# Revit family: Pump_Commercial-Sewage_Dewatering-Zoeller-X64HD_Single_Seal_4-HH-25-40BHP_Series
name_source: partatom
category: Mechanical Equipment
revit_build: Autodesk Revit 2014 (Build: 20130308_1515(x64)
units: mm (PartAtom-declared; Revit-internal decimal feet)

## types (9) — shared parameters
Assembly Code = D2090
Connection Description = 4" Horizontal Discharge
Default Elevation = 0"
Description = Heavy Duty Solids-Handling Pumps
Discharge Diameter = 4"
Discharge Radius = 2"
Flange = ANSI B16.1 CLASS 125
Height = 48 11/32"
Hertz = 60
High Temperature (5-10 BHP) = No
Impeller Type = 2 Vane Enclosed
Installation Type = Floor Mounted
Insulation = Class F
Inverted Duty = No
Inverted Duty Submersible = No
Length = 25 5/8"
Manufacturer = Zoeller
Material = Cast Iron-Zoeller-Powder Coated Epoxy
Max. Flow @ 117' = 0 GPM
Max. Flow @ 135' = 0 GPM
Max. Stator Temp. = 311 °F
Max. Water Temp. = 104 °F
Min. Recommended Fluid Level = 36"
Moisture Detection = Moisture Sensing Probes
Motor Design Letter = NEMA B
Motor Shaft = 416 SS
Motor Thermal Shutoff = Thermal Sensors With Automatic Reset
Motor Type = Standard Submersible
NEC Locked Rotor Code = F
O-Rings (Optional) Viton = No
O-Rings and Cover Gasket = Buna-N
Operation = Non-Automatic
Phase = 3
Power Cord = 25' (7.6 m) #2-4 SO
Price = Prices may vary. Please consult Manufacturer Representative for most up-to-date price list.
Product Documentation Link = https://www.zoellerengprod.com
Product Page URL = https://www.zoellerengprod.com
RPM = 1725
Sensor Cord Size = #16-5 SO
Service Factor = 1.15
Shaft Seal (Standard) = Carbon/Ceramic
Shaft Seal Lower (Options) = Silicon Carbide
Shaft Seal Upper (Options) = Silicon Carbide
Solid Size = 4"- 3-1/8"
Tandem Seals = Standard
Trimmed Impeller = No
URL = http://www.zoellerpumps.com
Warranty Information = 36 Months (Limited)
Waste Connection = Yes
Width = 22 1/2"

## per-type parameters (varying)
| type | Amps | Apparent Load | Flow Rate | Impeller Diameter | Locked Rotor Amps (Voltage Dependant) | Max. Flow @ 45' | Max. Flow @ 60' | Max. Flow @ 85' | Max. Head | Maximum KW Input | Model | Motor | Pump Net Weight: lbs. (kg) | Voltage |
| X6424 - 230V/3Ph/64.2A/25BHP | 64 A | 14766 VA | 1130 GPM | 9 7/8" | 349 | 1130 GPM | 0 GPM | 0 GPM | 110' | 21.1 | X6424 | 25 BHP | 705 lbs. (319 kg) | 230 V |
| X6425 - 230V/3Ph/79.8A/30BHP | 80 A | 18354 VA | 1100 GPM | 10 3/8" | 416 | 0 GPM | 1100 GPM | 0 GPM | 123' | 25.2 | X6425 | 30 BHP | 730 lbs. (331 kg) | 230 V |
| X6426 - 460V/3Ph/51.7A/40BHP | 52 A | 23782 VA | 1070 GPM | 11 3/8" | 257 | 0 GPM | 0 GPM | 1070 GPM | 142' | 33.5 | X6426 | 40 BHP | 780 lbs. (354 kg) | 460 V |
| X6424 - 460V/3Ph/32.1A/25BHP | 32 A | 14766 VA | 1130 GPM | 9 7/8" | 175 | 1130 GPM | 0 GPM | 0 GPM | 110' | 21.1 | X6424 | 25 BHP | 705 lbs. (319 kg) | 460 V |
| X6424 - 575V/3Ph/25.6A/25BHP | 26 A | 14720 VA | 1130 GPM | 9 7/8" | 140 | 1130 GPM | 0 GPM | 0 GPM | 110' | 21.1 | X6424 | 25 BHP | 705 lbs. (319 kg) | 575 V |
| X6425 - 460V/3Ph/39.9A/30BHP | 40 A | 18354 VA | 1100 GPM | 10 3/8" | 208 | 0 GPM | 1100 GPM | 0 GPM | 123' | 25.2 | X6425 | 30 BHP | 730 lbs. (331 kg) | 460 V |
| X6425 - 575V/3Ph/31.9A/30BHP | 32 A | 18343 VA | 1100 GPM | 10 3/8" | 166 | 0 GPM | 1100 GPM | 0 GPM | 123' | 25.2 | X6425 | 30 BHP | 730 lbs. (331 kg) | 575 V |
| X6426 - 230V/3Ph/103A/40BHP | 103 A | 23690 VA | 1070 GPM | 11 3/8" | 513 | 0 GPM | 0 GPM | 1070 GPM | 142' | 33.5 | X6426 | 40 BHP | 780 lbs. (354 kg) | 230 V |
| X6426 - 575V/3Ph/41.4A/40BHP | 41 A | 23805 VA | 1070 GPM | 11 3/8" | 205 | 0 GPM | 0 GPM | 1070 GPM | 142' | 33.5 | X6426 | 40 BHP | 780 lbs. (354 kg) | 575 V |

## geometry (parser evidence)
native form markers: Sweep x3
no freeform markers — native parametric forms only
